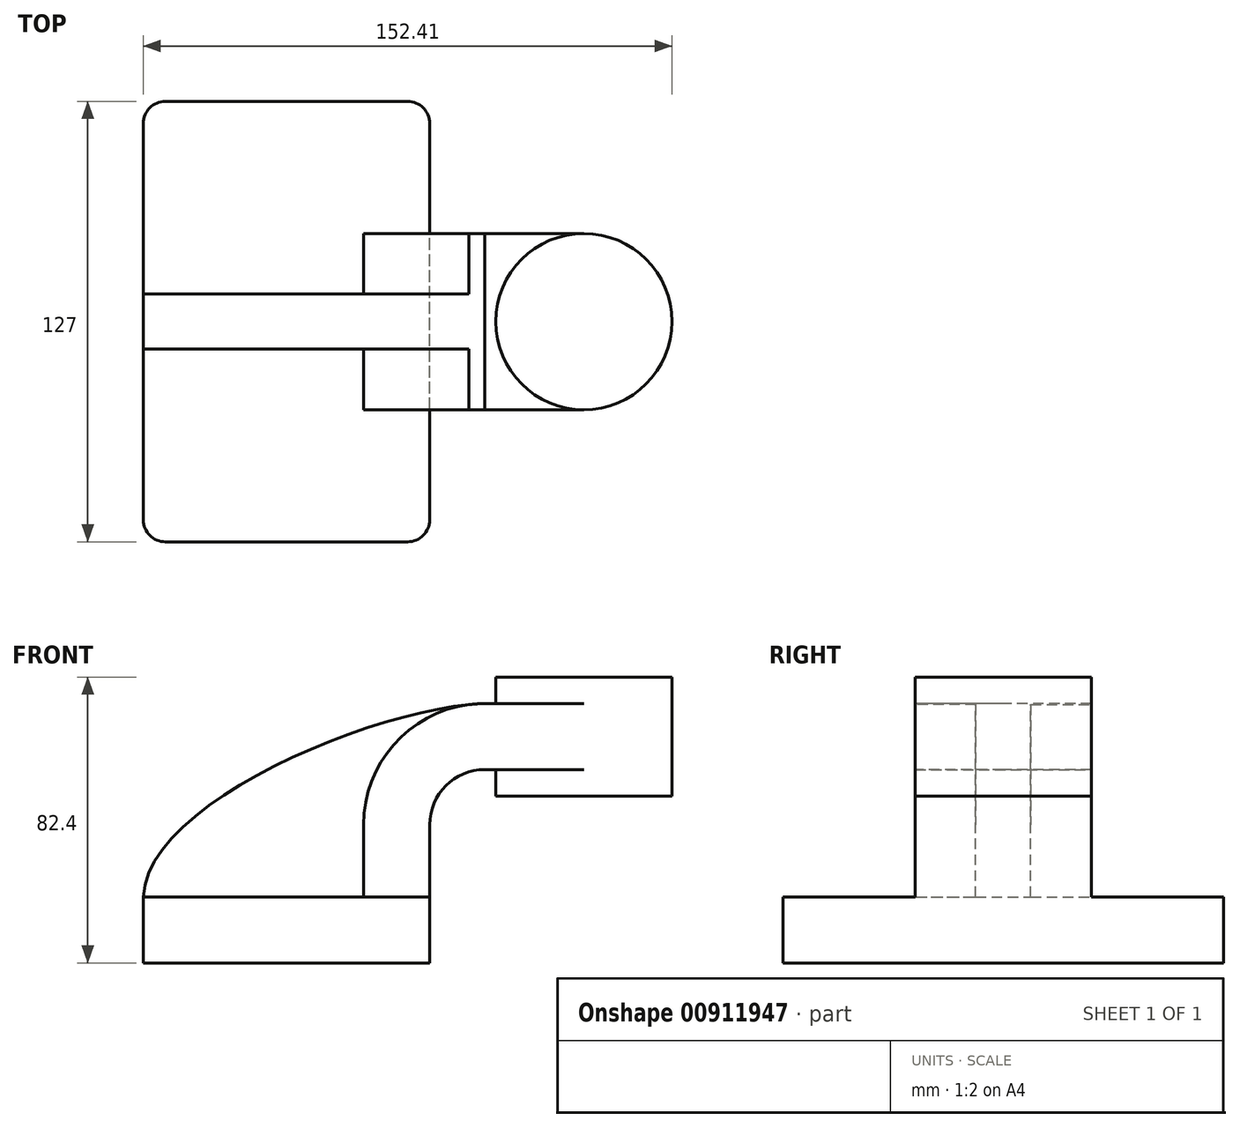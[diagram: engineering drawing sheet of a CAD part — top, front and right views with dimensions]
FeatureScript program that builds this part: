
annotation { "Feature Type Name" : "Feature", "Feature Type Description" : "" }
export const myFeature = defineFeature(function(context is Context, id is Id, definition is map)
    precondition{}
    {
        {
            var Q0;
            Q0=qCreatedBy(makeId("Front.planeOp"),FACE);
            var sketch = newSketch(context, id + "F0", { "sketchPlane" : qUnion([Q0])});
            skLineSegment(sketch, "E0.bottom", {"start": v(-41.28, 9.52) * mm, "end": v(41.28, 9.53) * mm});
            skLineSegment(sketch, "E0.top", {"start": v(-41.28, -9.53) * mm, "end": v(41.28, -9.53) * mm});
            skLineSegment(sketch, "E0.left", {"start": v(-41.28, 9.52) * mm, "end": v(-41.28, -9.53) * mm});
            skLineSegment(sketch, "E0.right", {"start": v(41.27, 9.53) * mm, "end": v(41.28, -9.52) * mm});
            skPoint(sketch, "E0.middle", {"position": v(0, 0) * mm});
            skLineSegment(sketch, "E1.bottom", {"start": v(111.13, 38.58) * mm, "end": v(60.33, 38.58) * mm});
            skLineSegment(sketch, "E1.left", {"start": v(111.13, 38.58) * mm, "end": v(111.13, 67.16) * mm});
            skLineSegment(sketch, "E1.right", {"start": v(60.33, 38.58) * mm, "end": v(60.33, 67.16) * mm});
            skPoint(sketch, "E1.middle", {"position": v(85.73, 52.87) * mm});
            skLineSegment(sketch, "E2", {"start": v(41.27, 9.53) * mm, "end": v(41.27, 30.33) * mm});
            skArc(sketch, "E3", {"start": v(41.27, 30.33) * mm, "mid": v(45.92, 41.55) * mm, "end": v(57.15, 46.2) * mm});
            skLineSegment(sketch, "E4", {"start": v(57.15, 46.2) * mm, "end": v(85.73, 46.2) * mm});
            skLineSegment(sketch, "E5.0", {"start": v(57.15, 65.25) * mm, "end": v(85.73, 65.25) * mm});
            skArc(sketch, "E5.1", {"start": v(22.22, 30.33) * mm, "mid": v(32.45, 55.02) * mm, "end": v(57.15, 65.25) * mm});
            skLineSegment(sketch, "E5.2", {"start": v(22.23, 9.53) * mm, "end": v(22.23, 30.33) * mm});
            skFitSpline(sketch, "E6", {"points": [v(-41.28, 9.53) * mm, v(57.15, 65.25) * mm], "startDerivative": vector(2.6, 82.42) * mm, "endDerivative": vector(90.83, 2.6) * mm});
            skLineSegment(sketch, "E7", {"start": v(85.73, 52.87) * mm, "end": v(85.73, 38.58) * mm});
            skLineSegment(sketch, "E8", {"start": v(85.73, 52.87) * mm, "end": v(85.73, 67.16) * mm});
            skLineSegment(sketch, "E9.MirrorCS", {"start": v(111.13, 72.87) * mm, "end": v(60.33, 72.87) * mm});
            skLineSegment(sketch, "E10.MirrorCS", {"start": v(60.33, 72.87) * mm, "end": v(60.33, 44.3) * mm});
            skLineSegment(sketch, "E11.MirrorCS", {"start": v(111.12, 72.87) * mm, "end": v(111.12, 44.3) * mm});
            skPoint(sketch, "E12.orphan", {"position": v(80.26, 65.25) * mm});
            skPoint(sketch, "E13.start.orphan", {"position": v(80.26, 46.2) * mm});
            skPoint(sketch, "E14.start.orphan", {"position": v(80.26, 55.73) * mm});
            skLineSegment(sketch, "E15", {"start": v(85.73, 67.16) * mm, "end": v(85.73, 72.87) * mm});
            skSolve(sketch);
        }
        {
            var Q0;
            Q0=makeQuery(id+"F0.imprint","IMPRINT",FACE,{"disambiguationData":[TD([[makeQuery(id+"F0.imprint","IMPRINT",EDGE,{"derivedFrom":sQuery(id+"F0.wireOp",EDGE,"E0.top")}),1.0]])]});
            extrude(context, id + "F1", {"entities" : qUnion([Q0]), "endBound" : BoundingType.SYMMETRIC, "depth" : 127 * mm, "offsetDistance" : 25.4 * mm});
        }
        {
            var Q0;
            {var subQ1=sQuery(id+"F0.wireOp",EDGE,"E2");Q0=makeQuery(id+"F0.imprint","IMPRINT",FACE,{"disambiguationData":[TD([[makeQuery(id+"F0.imprint","IMPRINT",EDGE,{"derivedFrom":subQ1}),1.0]])]});}
            var Q1;
            {var subQ0=sQuery(id+"F0.wireOp",EDGE,"E7");var subQ1=sQuery(id+"F0.wireOp",EDGE,"E4");var subQ2=makeQuery(id+"F0.imprint","INTERSECT",VERTEX,{"derivedFrom":[subQ1,subQ0]});Q1=makeQuery(id+"F0.imprint","IMPRINT",FACE,{"disambiguationData":[TD([[makeQuery(id+"F0.imprint","IMPRINT",EDGE,{"disambiguationData":[TD([[subQ2,1.0]])],"derivedFrom":subQ1}),1.0]])]});}
            extrude(context, id + "F2", {"entities" : qUnion([Q0, Q1]), "operationType" : NewBodyOperationType.ADD, "endBound" : BoundingType.SYMMETRIC, "depth" : 50.8 * mm, "offsetDistance" : 25.4 * mm});
        }
        {
            var Q0;
            {var subQ3=sQuery(id+"F0.wireOp",EDGE,"E5.2");Q0=makeQuery(id+"F0.imprint","IMPRINT",FACE,{"disambiguationData":[TD([[makeQuery(id+"F0.imprint","IMPRINT",EDGE,{"derivedFrom":subQ3}),1.0]])]});}
            extrude(context, id + "F3", {"entities" : qUnion([Q0]), "operationType" : NewBodyOperationType.ADD, "endBound" : BoundingType.SYMMETRIC, "depth" : 15.88 * mm, "offsetDistance" : 25.4 * mm});
        }
        {
            var Q0;
            {var subQ4=sQuery(id+"F0.wireOp",EDGE,"E1.left");Q0=makeQuery(id+"F0.imprint","IMPRINT",FACE,{"disambiguationData":[TD([[makeQuery(id+"F0.imprint","IMPRINT",EDGE,{"derivedFrom":subQ4}),1.0]])]});}
            var Q1;
            Q1=sQuery(id+"F0.wireOp",EDGE,"E8");
            revolve(context, id + "F4", {"operationType" : NewBodyOperationType.ADD, "surfaceOperationType" : NewSurfaceOperationType.NEW, "entities" : qUnion([Q0]), "axis" : qUnion([Q1]), "revolveType" : RevolveType.FULL});
        }
        {
            var Q0;
            Q0=makeQuery(id+"F1.opExtrude","CAP_EDGE",EDGE,{"disambiguationData":[OSD([sQuery(id+"F0.wireOp",EDGE,"E0.right")])],"isStart":false});
            var Q1;
            Q1=makeQuery(id+"F1.opExtrude","CAP_EDGE",EDGE,{"disambiguationData":[OSD([sQuery(id+"F0.wireOp",EDGE,"E0.right")])],"isStart":true});
            var Q2;
            Q2=makeQuery(id+"F1.opExtrude","CAP_EDGE",EDGE,{"disambiguationData":[OSD([sQuery(id+"F0.wireOp",EDGE,"E0.left")])],"isStart":true});
            var Q3;
            Q3=makeQuery(id+"F1.opExtrude","CAP_EDGE",EDGE,{"disambiguationData":[OSD([sQuery(id+"F0.wireOp",EDGE,"E0.left")])],"isStart":false});
            fillet(context, id + "F5", {"entities" : qUnion([Q0, Q1, Q2, Q3]), "radius" : 6.35 * mm, "tangentPropagation" : true, "allowEdgeOverflow" : false});
        }
    });
